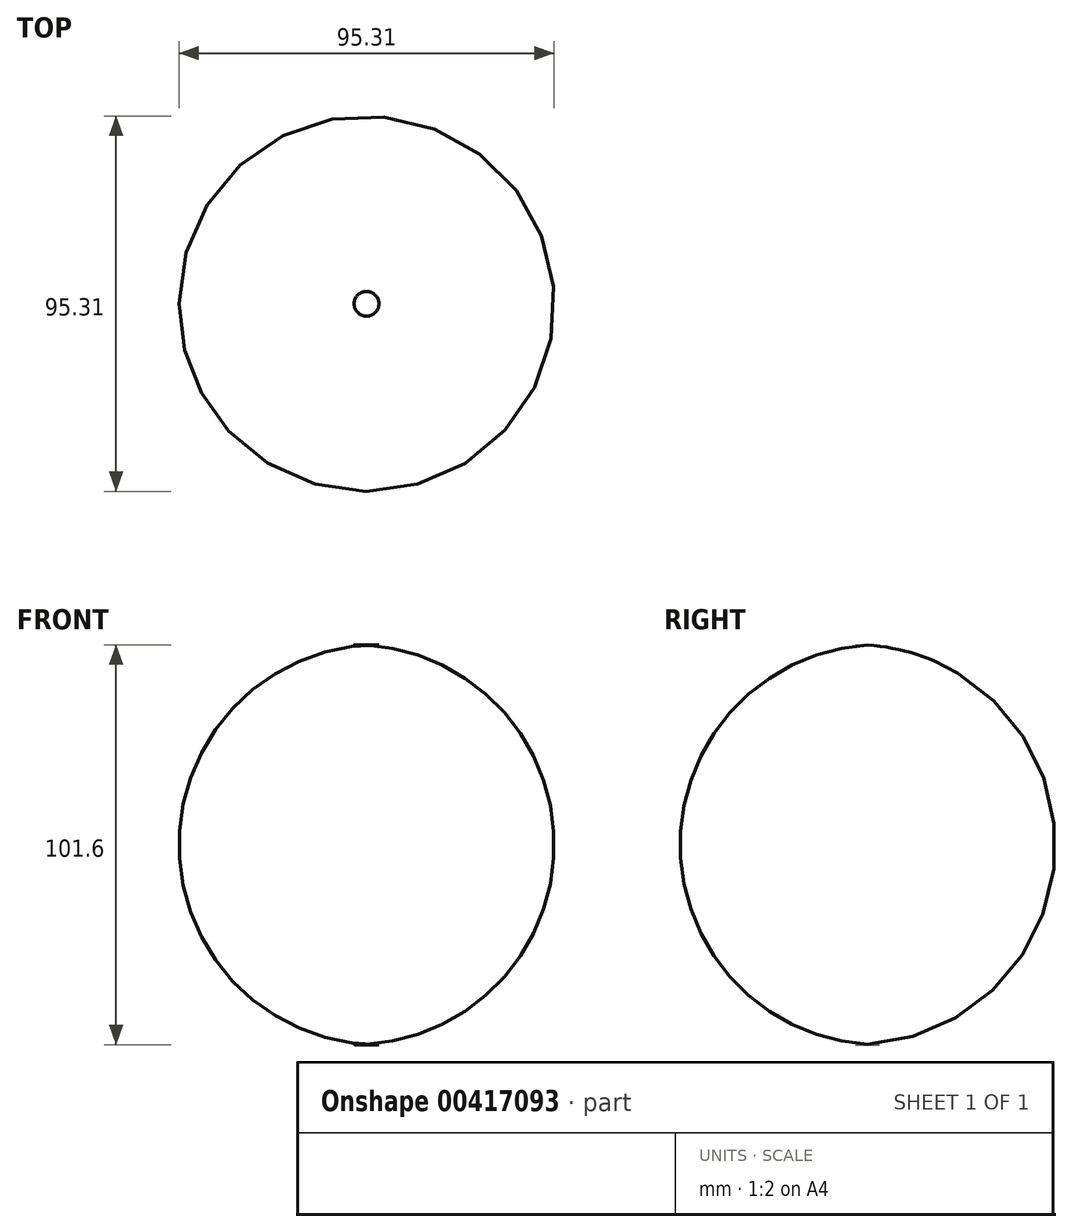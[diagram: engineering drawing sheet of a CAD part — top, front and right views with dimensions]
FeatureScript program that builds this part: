
annotation { "Feature Type Name" : "Feature", "Feature Type Description" : "" }
export const myFeature = defineFeature(function(context is Context, id is Id, definition is map)
    precondition{}
    {
        {
            var Q0;
            Q0=qCreatedBy(makeId("Top.planeOp"),FACE);
            var sketch = newSketch(context, id + "F0", { "sketchPlane" : qUnion([Q0])});
            skCircle(sketch, "E0", {"center": v(-0.17, -0.17) * mm, "radius": 53.95 * mm});
            skSolve(sketch);
        }
        {
            var Q0;
            Q0=makeQuery(id+"F0.imprint","IMPRINT",FACE,{"disambiguationData":[TD([[makeQuery(id+"F0.imprint","IMPRINT",EDGE,{"derivedFrom":sQuery(id+"F0.wireOp",EDGE,"E0")}),1.0]])]});
            extrude(context, id + "F1", {"entities" : qUnion([Q0]), "depth" : 101.6 * mm});
        }
        {
            var Q0;
            Q0=makeQuery(id+"F1.opExtrude","CAP_EDGE",EDGE,{"disambiguationData":[OSD([sQuery(id+"F0.wireOp",EDGE,"E0")])],"isStart":false});
            var Q1;
            Q1=makeQuery(id+"F1.opExtrude","CAP_EDGE",EDGE,{"disambiguationData":[OSD([sQuery(id+"F0.wireOp",EDGE,"E0")])],"isStart":true});
            fillet(context, id + "F2", {"entities" : qUnion([Q0, Q1]), "radius" : 50.8 * mm, "allowEdgeOverflow" : false});
        }
    });
